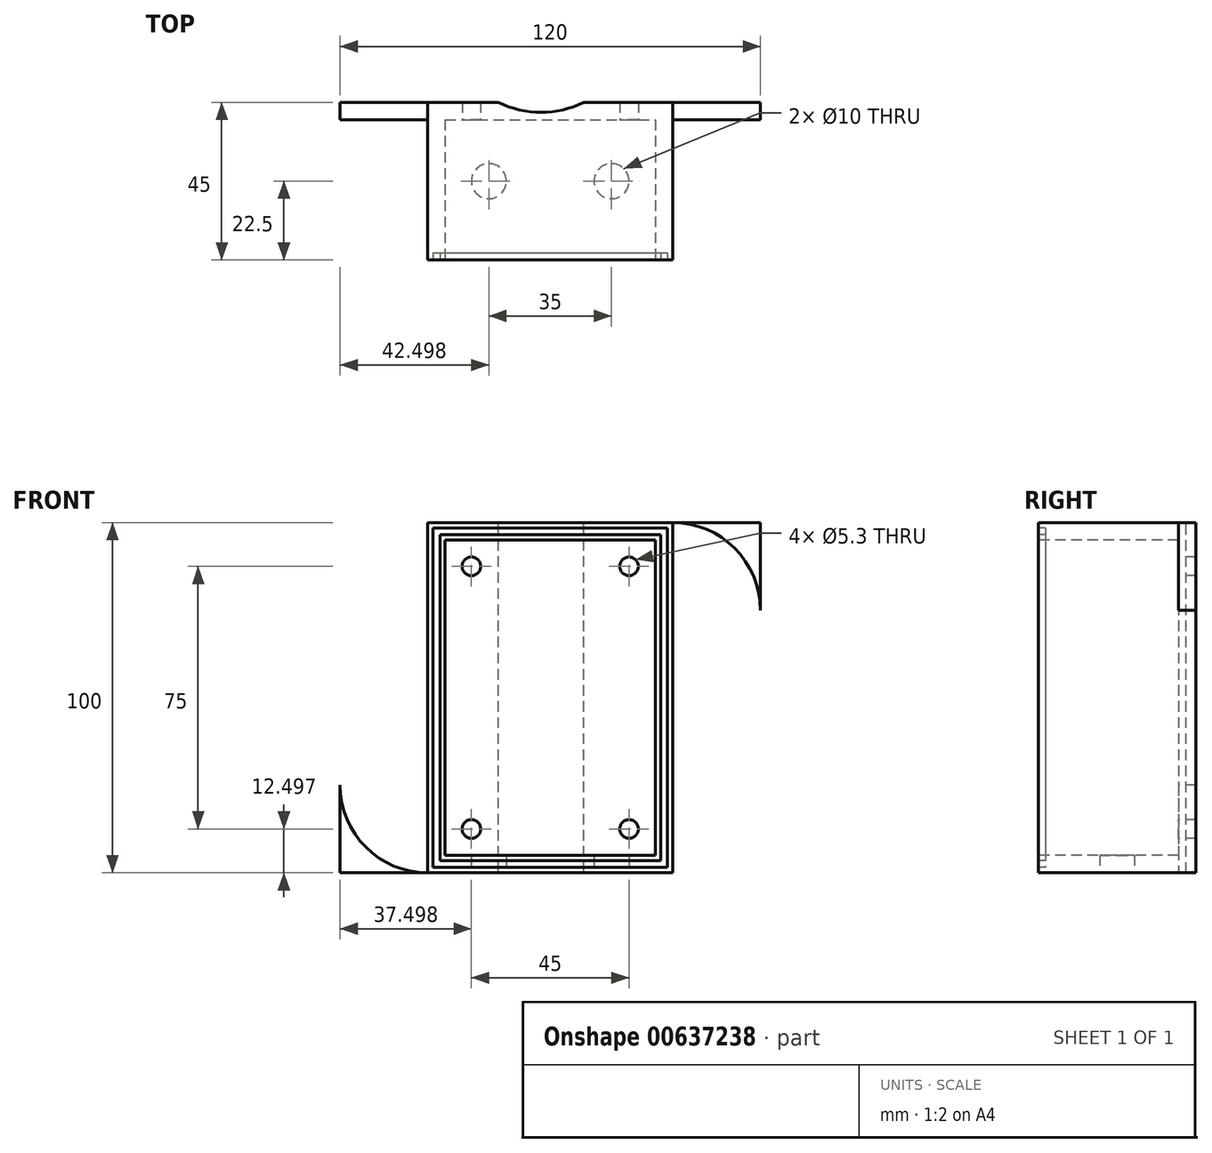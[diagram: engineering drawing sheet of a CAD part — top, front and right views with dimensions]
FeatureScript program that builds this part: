
annotation { "Feature Type Name" : "Feature", "Feature Type Description" : "" }
export const myFeature = defineFeature(function(context is Context, id is Id, definition is map)
    precondition{}
    {
        {
            var Q0;
            Q0=qCreatedBy(makeId("Front.planeOp"),FACE);
            var sketch = newSketch(context, id + "F0", { "sketchPlane" : qUnion([Q0])});
            skLineSegment(sketch, "E0.bottom", {"start": v(-22.3, 41.75) * mm, "end": v(47.7, 41.75) * mm});
            skLineSegment(sketch, "E0.top", {"start": v(-22.3, -58.25) * mm, "end": v(47.7, -58.25) * mm});
            skLineSegment(sketch, "E0.left", {"start": v(-22.3, 41.75) * mm, "end": v(-22.3, -58.25) * mm});
            skLineSegment(sketch, "E0.right", {"start": v(47.7, 41.75) * mm, "end": v(47.7, -58.25) * mm});
            skSolve(sketch);
        }
        {
            var Q0;
            Q0=makeQuery(id+"F0.imprint","IMPRINT",FACE,{"disambiguationData":[TD([[makeQuery(id+"F0.imprint","IMPRINT",EDGE,{"derivedFrom":sQuery(id+"F0.wireOp",EDGE,"E0.bottom")}),-1.0]])]});
            extrude(context, id + "F1", {"entities" : qUnion([Q0]), "depth" : 45 * mm, "offsetDistance" : 25 * mm});
        }
        {
            var Q0;
            Q0=makeQuery(id+"F1.opExtrude","CAP_FACE",FACE,{"disambiguationData":[OSD([sQuery(id+"F0.wireOp",EDGE,"E0.bottom"),sQuery(id+"F0.wireOp",EDGE,"E0.top"),sQuery(id+"F0.wireOp",EDGE,"E0.left"),sQuery(id+"F0.wireOp",EDGE,"E0.right")])],"isStart":false});
            var sketch = newSketch(context, id + "F2", { "sketchPlane" : qUnion([Q0])});
            skLineSegment(sketch, "E1.bottom", {"start": v(-17.3, 36.75) * mm, "end": v(42.7, 36.75) * mm});
            skLineSegment(sketch, "E1.top", {"start": v(-17.3, -53.25) * mm, "end": v(42.7, -53.25) * mm});
            skLineSegment(sketch, "E1.left", {"start": v(-17.3, 36.75) * mm, "end": v(-17.3, -53.25) * mm});
            skLineSegment(sketch, "E1.right", {"start": v(42.7, 36.75) * mm, "end": v(42.7, -53.25) * mm});
            skSolve(sketch);
        }
        {
            var Q0;
            Q0=makeQuery(id+"F2.imprint","IMPRINT",FACE,{"disambiguationData":[TD([[makeQuery(id+"F2.imprint","IMPRINT",EDGE,{"derivedFrom":sQuery(id+"F2.wireOp",EDGE,"E1.bottom")}),-1.0]])]});
            extrude(context, id + "F3", {"entities" : qUnion([Q0]), "operationType" : NewBodyOperationType.REMOVE, "oppositeDirection" : true, "depth" : 40 * mm, "offsetDistance" : 25 * mm});
        }
        {
            var Q0;
            Q0=makeQuery(id+"F3.boolean.opBoolean","COPY",FACE,{"derivedFrom":makeQuery(id+"F3.opExtrude","CAP_FACE",FACE,{"disambiguationData":[OSD([sQuery(id+"F2.wireOp",EDGE,"E1.bottom"),sQuery(id+"F2.wireOp",EDGE,"E1.top"),sQuery(id+"F2.wireOp",EDGE,"E1.left"),sQuery(id+"F2.wireOp",EDGE,"E1.right")])],"isStart":false})});
            var sketch = newSketch(context, id + "F4", { "sketchPlane" : qUnion([Q0])});
            skCircle(sketch, "E2", {"center": v(-9.8, 29.25) * mm, "radius": 2.65 * mm});
            skCircle(sketch, "E3", {"center": v(35.2, 29.25) * mm, "radius": 2.65 * mm});
            skCircle(sketch, "E4", {"center": v(35.2, -45.75) * mm, "radius": 2.65 * mm});
            skCircle(sketch, "E5", {"center": v(-9.8, -45.75) * mm, "radius": 2.65 * mm});
            skSolve(sketch);
        }
        {
            var Q0;
            Q0=makeQuery(id+"F4.imprint","IMPRINT",FACE,{"disambiguationData":[TD([[makeQuery(id+"F4.imprint","IMPRINT",EDGE,{"derivedFrom":sQuery(id+"F4.wireOp",EDGE,"E2")}),1.0]])]});
            var Q1;
            Q1=sQuery(id+"F4.wireOp",EDGE,"E2");
            extrude(context, id + "F5", {"entities" : qUnion([Q0]), "operationType" : NewBodyOperationType.REMOVE, "surfaceEntities" : qUnion([Q1]), "oppositeDirection" : true, "depth" : 5 * mm, "offsetDistance" : 25 * mm});
        }
        {
            var Q0;
            Q0=makeQuery(id+"F4.imprint","IMPRINT",FACE,{"disambiguationData":[TD([[makeQuery(id+"F4.imprint","IMPRINT",EDGE,{"derivedFrom":sQuery(id+"F4.wireOp",EDGE,"E3")}),1.0]])]});
            var Q1;
            Q1=sQuery(id+"F4.wireOp",EDGE,"E3");
            var Q2;
            Q2=sQuery(id+"F4.wireOp",EDGE,"E5");
            var Q3;
            Q3=sQuery(id+"F4.wireOp",EDGE,"E4");
            extrude(context, id + "F6", {"entities" : qUnion([Q0]), "operationType" : NewBodyOperationType.REMOVE, "surfaceEntities" : qUnion([Q1, Q2, Q3]), "oppositeDirection" : true, "depth" : 25 * mm, "offsetDistance" : 25 * mm});
        }
        {
            var Q0;
            Q0=makeQuery(id+"F4.imprint","IMPRINT",FACE,{"disambiguationData":[TD([[makeQuery(id+"F4.imprint","IMPRINT",EDGE,{"derivedFrom":sQuery(id+"F4.wireOp",EDGE,"E4")}),1.0]])]});
            var Q1;
            Q1=sQuery(id+"F4.wireOp",EDGE,"E4");
            extrude(context, id + "F7", {"entities" : qUnion([Q0]), "operationType" : NewBodyOperationType.REMOVE, "surfaceEntities" : qUnion([Q1]), "oppositeDirection" : true, "depth" : 25 * mm, "offsetDistance" : 25 * mm});
        }
        {
            var Q0;
            Q0=makeQuery(id+"F4.imprint","IMPRINT",FACE,{"disambiguationData":[TD([[makeQuery(id+"F4.imprint","IMPRINT",EDGE,{"derivedFrom":sQuery(id+"F4.wireOp",EDGE,"E5")}),1.0]])]});
            var Q1;
            Q1=sQuery(id+"F4.wireOp",EDGE,"E5");
            extrude(context, id + "F8", {"entities" : qUnion([Q0]), "operationType" : NewBodyOperationType.REMOVE, "surfaceEntities" : qUnion([Q1]), "oppositeDirection" : true, "depth" : 25 * mm, "offsetDistance" : 25 * mm});
        }
        {
            var Q0;
            Q0=makeQuery(id+"F1.opExtrude","SWEPT_FACE",FACE,{"disambiguationData":[OSD([sQuery(id+"F0.wireOp",EDGE,"E0.left")])]});
            var sketch = newSketch(context, id + "F9", { "sketchPlane" : qUnion([Q0])});
            skLineSegment(sketch, "E6.bottom", {"start": v(0, 41.75) * mm, "end": v(5, 41.75) * mm});
            skLineSegment(sketch, "E6.top", {"start": v(0, -58.25) * mm, "end": v(5, -58.25) * mm});
            skLineSegment(sketch, "E6.left", {"start": v(0, 41.75) * mm, "end": v(0, -58.25) * mm});
            skLineSegment(sketch, "E6.right", {"start": v(5, 41.75) * mm, "end": v(5, -58.25) * mm});
            skSolve(sketch);
        }
        {
            var Q0;
            Q0=makeQuery(id+"F9.imprint","IMPRINT",FACE,{"disambiguationData":[TD([[makeQuery(id+"F9.imprint","IMPRINT",EDGE,{"derivedFrom":sQuery(id+"F9.wireOp",EDGE,"E6.bottom")}),1.0]])]});
            extrude(context, id + "F10", {"entities" : qUnion([Q0]), "operationType" : NewBodyOperationType.ADD, "depth" : 25 * mm, "offsetDistance" : 25 * mm});
        }
        {
            var Q0;
            Q0=makeQuery(id+"F1.opExtrude","SWEPT_FACE",FACE,{"disambiguationData":[OSD([sQuery(id+"F0.wireOp",EDGE,"E0.right")])]});
            var sketch = newSketch(context, id + "F11", { "sketchPlane" : qUnion([Q0])});
            skLineSegment(sketch, "E7.bottom", {"start": v(0, 41.75) * mm, "end": v(-5, 41.75) * mm});
            skLineSegment(sketch, "E7.top", {"start": v(0, -58.25) * mm, "end": v(-5, -58.25) * mm});
            skLineSegment(sketch, "E7.left", {"start": v(0, 41.75) * mm, "end": v(0, -58.25) * mm});
            skLineSegment(sketch, "E7.right", {"start": v(-5, 41.75) * mm, "end": v(-5, -58.25) * mm});
            skSolve(sketch);
        }
        {
            var Q0;
            Q0=makeQuery(id+"F11.imprint","IMPRINT",FACE,{"disambiguationData":[TD([[makeQuery(id+"F11.imprint","IMPRINT",EDGE,{"derivedFrom":sQuery(id+"F11.wireOp",EDGE,"E7.bottom")}),-1.0]])]});
            extrude(context, id + "F12", {"entities" : qUnion([Q0]), "operationType" : NewBodyOperationType.ADD, "depth" : 25 * mm, "offsetDistance" : 25 * mm});
        }
        {
            var Q0;
            Q0=makeQuery(id+"F10.opExtrude","SWEPT_FACE",FACE,{"disambiguationData":[OSD([sQuery(id+"F9.wireOp",EDGE,"E6.right")])]});
            var sketch = newSketch(context, id + "F13", { "sketchPlane" : qUnion([Q0])});
            skArc(sketch, "E8", {"start": v(-22.3, 41.75) * mm, "mid": v(-39.97, 34.42) * mm, "end": v(-47.3, 16.75) * mm});
            skArc(sketch, "E9", {"start": v(-22.3, -58.25) * mm, "mid": v(-39.97, -50.93) * mm, "end": v(-47.3, -33.25) * mm});
            skLineSegment(sketch, "E10.top", {"start": v(-42.3, 6.75) * mm, "end": v(-37.3, 6.75) * mm});
            skLineSegment(sketch, "E11.top", {"start": v(-32.3, 6.75) * mm, "end": v(-27.3, 6.75) * mm});
            skLineSegment(sketch, "E12", {"start": v(-42.3, 6.75) * mm, "end": v(-42.3, -23.25) * mm});
            skLineSegment(sketch, "E13", {"start": v(-42.3, -23.25) * mm, "end": v(-37.29, -23.25) * mm});
            skLineSegment(sketch, "E14", {"start": v(-37.3, 6.75) * mm, "end": v(-37.29, -23.25) * mm});
            skLineSegment(sketch, "E15", {"start": v(-32.3, 6.75) * mm, "end": v(-32.3, -23.25) * mm});
            skLineSegment(sketch, "E16", {"start": v(-27.3, 6.75) * mm, "end": v(-27.3, -23.25) * mm});
            skLineSegment(sketch, "E17", {"start": v(-32.3, -23.25) * mm, "end": v(-27.3, -23.25) * mm});
            skSolve(sketch);
        }
        {
            var Q0;
            {var subQ0=sQuery(id+"F13.wireOp",EDGE,"E8");Q0=makeQuery(id+"F13.imprint","IMPRINT",FACE,{"disambiguationData":[TD([[makeQuery(id+"F13.imprint","IMPRINT",EDGE,{"derivedFrom":subQ0}),-1.0]])]});}
            extrude(context, id + "F14", {"entities" : qUnion([Q0]), "operationType" : NewBodyOperationType.REMOVE, "oppositeDirection" : true, "depth" : 25 * mm, "offsetDistance" : 25 * mm});
        }
        {
            var Q0;
            {var subQ0=sQuery(id+"F13.wireOp",EDGE,"E9");Q0=makeQuery(id+"F13.imprint","IMPRINT",FACE,{"disambiguationData":[TD([[makeQuery(id+"F13.imprint","IMPRINT",EDGE,{"derivedFrom":subQ0}),1.0]])]});}
            extrude(context, id + "F15", {"entities" : qUnion([Q0]), "operationType" : NewBodyOperationType.REMOVE, "oppositeDirection" : true, "depth" : 25 * mm, "offsetDistance" : 25 * mm});
        }
        {
            var Q0;
            Q0=makeQuery(id+"F12.opExtrude","SWEPT_FACE",FACE,{"disambiguationData":[OSD([sQuery(id+"F11.wireOp",EDGE,"E7.right")])]});
            var sketch = newSketch(context, id + "F16", { "sketchPlane" : qUnion([Q0])});
            skArc(sketch, "E18", {"start": v(47.7, 41.75) * mm, "mid": v(65.39, 34.42) * mm, "end": v(72.7, 16.75) * mm});
            skArc(sketch, "E19", {"start": v(47.7, -58.25) * mm, "mid": v(65.39, -50.93) * mm, "end": v(72.7, -33.25) * mm});
            skLineSegment(sketch, "E20.bottom", {"start": v(67.7, 6.75) * mm, "end": v(62.7, 6.75) * mm});
            skLineSegment(sketch, "E20.top", {"start": v(67.7, -23.25) * mm, "end": v(62.7, -23.25) * mm});
            skLineSegment(sketch, "E20.left", {"start": v(67.7, 6.75) * mm, "end": v(67.7, -23.25) * mm});
            skLineSegment(sketch, "E20.right", {"start": v(62.7, 6.75) * mm, "end": v(62.7, -23.25) * mm});
            skLineSegment(sketch, "E21.bottom", {"start": v(57.7, 6.75) * mm, "end": v(52.7, 6.75) * mm});
            skLineSegment(sketch, "E21.top", {"start": v(57.7, -23.25) * mm, "end": v(52.7, -23.25) * mm});
            skLineSegment(sketch, "E21.left", {"start": v(57.7, 6.75) * mm, "end": v(57.7, -23.25) * mm});
            skLineSegment(sketch, "E21.right", {"start": v(52.7, 6.75) * mm, "end": v(52.7, -23.25) * mm});
            skSolve(sketch);
        }
        {
            var Q0;
            {var subQ0=sQuery(id+"F16.wireOp",EDGE,"E18");Q0=makeQuery(id+"F16.imprint","IMPRINT",FACE,{"disambiguationData":[TD([[makeQuery(id+"F16.imprint","IMPRINT",EDGE,{"derivedFrom":subQ0}),1.0]])]});}
            var Q1;
            {var subQ0=sQuery(id+"F16.wireOp",EDGE,"E19");Q1=makeQuery(id+"F16.imprint","IMPRINT",FACE,{"disambiguationData":[TD([[makeQuery(id+"F16.imprint","IMPRINT",EDGE,{"derivedFrom":subQ0}),-1.0]])]});}
            extrude(context, id + "F17", {"entities" : qUnion([Q0, Q1]), "operationType" : NewBodyOperationType.REMOVE, "oppositeDirection" : true, "depth" : 25 * mm, "offsetDistance" : 25 * mm});
        }
        {
            var Q0;
            Q0=makeQuery(id+"F1.opExtrude","CAP_FACE",FACE,{"disambiguationData":[OSD([sQuery(id+"F0.wireOp",EDGE,"E0.bottom"),sQuery(id+"F0.wireOp",EDGE,"E0.top"),sQuery(id+"F0.wireOp",EDGE,"E0.left"),sQuery(id+"F0.wireOp",EDGE,"E0.right")])],"isStart":false});
            var sketch = newSketch(context, id + "F18", { "sketchPlane" : qUnion([Q0])});
            skLineSegment(sketch, "E22.top", {"start": v(-20.8, -56.75) * mm, "end": v(46.2, -56.75) * mm});
            skLineSegment(sketch, "E22.left", {"start": v(-20.8, 40.25) * mm, "end": v(-20.8, -56.75) * mm});
            skLineSegment(sketch, "E22.right", {"start": v(46.2, 40.25) * mm, "end": v(46.2, -56.75) * mm});
            skLineSegment(sketch, "E23.bottom", {"start": v(-18.8, 38.25) * mm, "end": v(44.2, 38.25) * mm});
            skLineSegment(sketch, "E23.top", {"start": v(-18.8, -54.75) * mm, "end": v(44.2, -54.75) * mm});
            skLineSegment(sketch, "E24", {"start": v(-18.8, 38.25) * mm, "end": v(-18.8, -54.75) * mm});
            skLineSegment(sketch, "E25", {"start": v(-20.8, 40.25) * mm, "end": v(46.2, 40.25) * mm});
            skLineSegment(sketch, "E26", {"start": v(44.2, 38.25) * mm, "end": v(44.2, -54.75) * mm});
            skSolve(sketch);
        }
        {
            var Q0;
            Q0=makeQuery(id+"F18.imprint","IMPRINT",FACE,{"disambiguationData":[TD([[makeQuery(id+"F18.imprint","IMPRINT",EDGE,{"derivedFrom":sQuery(id+"F18.wireOp",EDGE,"E22.top")}),1.0]])]});
            extrude(context, id + "F19", {"entities" : qUnion([Q0]), "operationType" : NewBodyOperationType.REMOVE, "oppositeDirection" : true, "depth" : 2 * mm, "offsetDistance" : 25 * mm});
        }
        {
            var Q0;
            Q0=makeQuery(id+"F13.imprint","IMPRINT",FACE,{"disambiguationData":[TD([[makeQuery(id+"F13.imprint","IMPRINT",EDGE,{"derivedFrom":sQuery(id+"F13.wireOp",EDGE,"E10.top")}),-1.0]])]});
            var Q1;
            Q1=makeQuery(id+"F13.imprint","IMPRINT",FACE,{"disambiguationData":[TD([[makeQuery(id+"F13.imprint","IMPRINT",EDGE,{"derivedFrom":sQuery(id+"F13.wireOp",EDGE,"E11.top")}),-1.0]])]});
            extrude(context, id + "F20", {"entities" : qUnion([Q0, Q1]), "operationType" : NewBodyOperationType.REMOVE, "oppositeDirection" : true, "depth" : 25 * mm, "offsetDistance" : 25 * mm});
        }
        {
            var Q0;
            Q0=makeQuery(id+"F16.imprint","IMPRINT",FACE,{"disambiguationData":[TD([[makeQuery(id+"F16.imprint","IMPRINT",EDGE,{"derivedFrom":sQuery(id+"F16.wireOp",EDGE,"E21.bottom")}),1.0]])]});
            var Q1;
            Q1=makeQuery(id+"F16.imprint","IMPRINT",FACE,{"disambiguationData":[TD([[makeQuery(id+"F16.imprint","IMPRINT",EDGE,{"derivedFrom":sQuery(id+"F16.wireOp",EDGE,"E20.bottom")}),1.0]])]});
            extrude(context, id + "F21", {"entities" : qUnion([Q0, Q1]), "operationType" : NewBodyOperationType.REMOVE, "oppositeDirection" : true, "depth" : 25 * mm, "offsetDistance" : 25 * mm});
        }
        {
            var Q0;
            Q0=makeQuery(id+"F12.boolean.opBoolean","MERGE",FACE,{"derivedFrom":[makeQuery(id+"F10.boolean.opBoolean","MERGE",FACE,{"derivedFrom":[makeQuery(id+"F1.opExtrude","SWEPT_FACE",FACE,{"disambiguationData":[OSD([sQuery(id+"F0.wireOp",EDGE,"E0.top")])]}),makeQuery(id+"F10.opExtrude","SWEPT_FACE",FACE,{"disambiguationData":[OSD([sQuery(id+"F9.wireOp",EDGE,"E6.top")])]})]}),makeQuery(id+"F12.opExtrude","SWEPT_FACE",FACE,{"disambiguationData":[OSD([sQuery(id+"F11.wireOp",EDGE,"E7.top")])]})]});
            var sketch = newSketch(context, id + "F22", { "sketchPlane" : qUnion([Q0])});
            skLineSegment(sketch, "E27", {"start": v(47.7, 0) * mm, "end": v(47.7, 45) * mm});
            skCircle(sketch, "E28", {"center": v(-4.8, 22.5) * mm, "radius": 5 * mm});
            skCircle(sketch, "E29", {"center": v(30.2, 22.5) * mm, "radius": 5 * mm});
            skSolve(sketch);
        }
        {
            var Q0;
            Q0=makeQuery(id+"F22.imprint","IMPRINT",FACE,{"disambiguationData":[TD([[makeQuery(id+"F22.imprint","IMPRINT",EDGE,{"derivedFrom":sQuery(id+"F22.wireOp",EDGE,"E29")}),1.0]])]});
            var Q1;
            Q1=makeQuery(id+"F22.imprint","IMPRINT",FACE,{"disambiguationData":[TD([[makeQuery(id+"F22.imprint","IMPRINT",EDGE,{"derivedFrom":sQuery(id+"F22.wireOp",EDGE,"E28")}),1.0]])]});
            extrude(context, id + "F23", {"entities" : qUnion([Q0, Q1]), "operationType" : NewBodyOperationType.REMOVE, "oppositeDirection" : true, "depth" : 25 * mm, "offsetDistance" : 25 * mm});
        }
        {
            var Q0;
            Q0=makeQuery(id+"F12.boolean.opBoolean","MERGE",FACE,{"derivedFrom":[makeQuery(id+"F10.boolean.opBoolean","MERGE",FACE,{"derivedFrom":[makeQuery(id+"F1.opExtrude","SWEPT_FACE",FACE,{"disambiguationData":[OSD([sQuery(id+"F0.wireOp",EDGE,"E0.bottom")])]}),makeQuery(id+"F10.opExtrude","SWEPT_FACE",FACE,{"disambiguationData":[OSD([sQuery(id+"F9.wireOp",EDGE,"E6.bottom")])]})]}),makeQuery(id+"F12.opExtrude","SWEPT_FACE",FACE,{"disambiguationData":[OSD([sQuery(id+"F11.wireOp",EDGE,"E7.bottom")])]})]});
            var sketch = newSketch(context, id + "F24", { "sketchPlane" : qUnion([Q0])});
            skArc(sketch, "E30", {"start": v(-2.05, 0) * mm, "mid": v(10.1, -2.84) * mm, "end": v(22.27, 0) * mm});
            skLineSegment(sketch, "E31", {"start": v(-2.05, 0) * mm, "end": v(22.27, 0) * mm});
            skSolve(sketch);
        }
        {
            var Q0;
            Q0=makeQuery(id+"F24.imprint","IMPRINT",FACE,{"disambiguationData":[TD([[makeQuery(id+"F24.imprint","IMPRINT",EDGE,{"derivedFrom":sQuery(id+"F24.wireOp",EDGE,"E30")}),1.0]])]});
            extrude(context, id + "F25", {"entities" : qUnion([Q0]), "operationType" : NewBodyOperationType.REMOVE, "oppositeDirection" : true, "depth" : 100 * mm, "offsetDistance" : 25 * mm});
        }
    });
